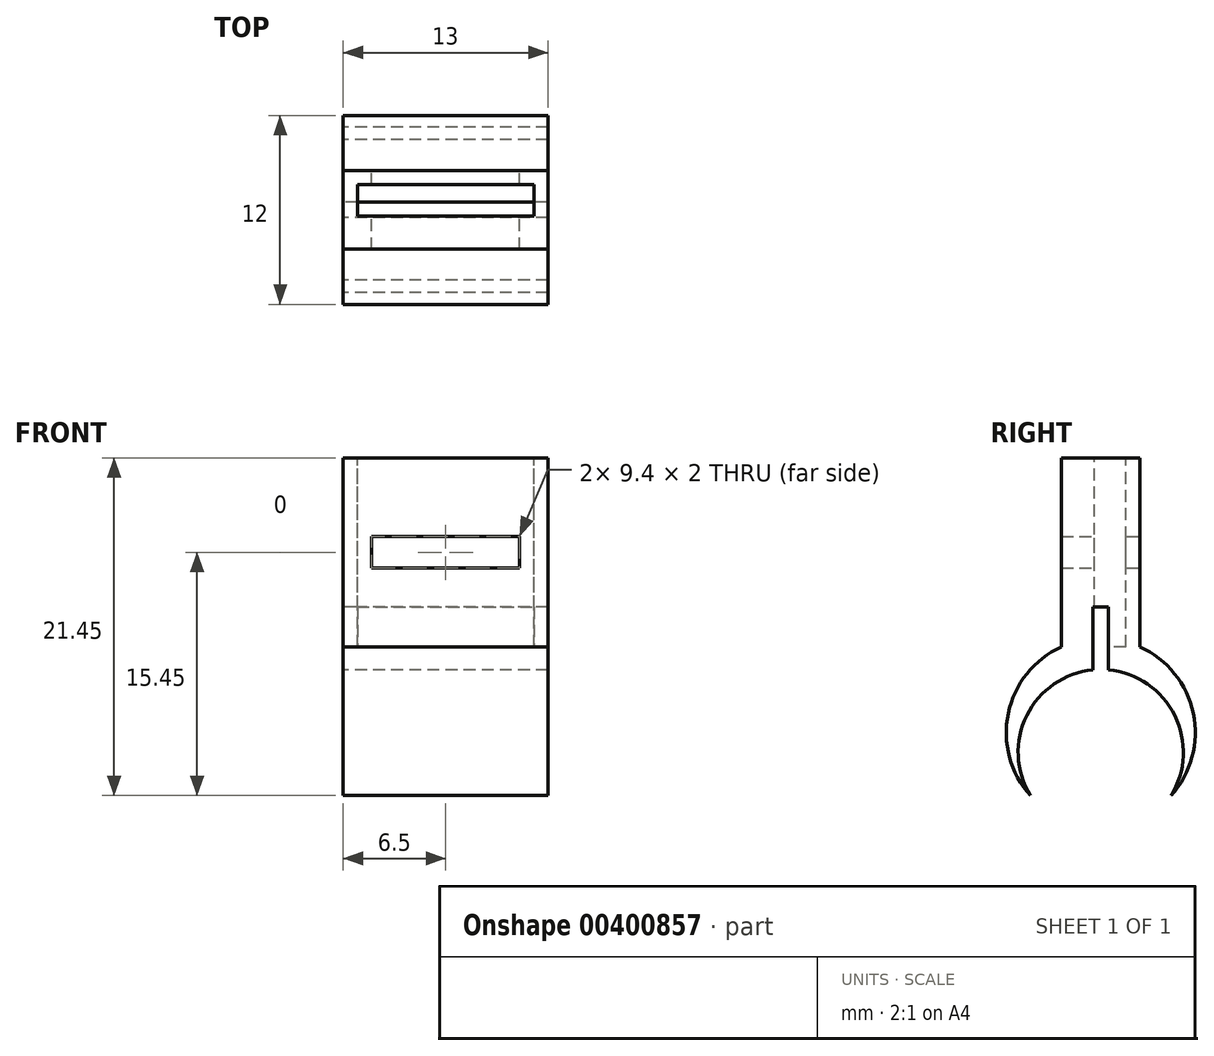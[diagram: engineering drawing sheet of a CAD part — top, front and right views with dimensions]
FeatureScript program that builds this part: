
annotation { "Feature Type Name" : "Feature", "Feature Type Description" : "" }
export const myFeature = defineFeature(function(context is Context, id is Id, definition is map)
    precondition{}
    {
        {
            var Q0;
            Q0=qCreatedBy(makeId("Top.planeOp"),FACE);
            var sketch = newSketch(context, id + "F0", { "sketchPlane" : qUnion([Q0])});
            skLineSegment(sketch, "E0.bottom", {"start": v(-6.5, 2.5) * mm, "end": v(6.5, 2.5) * mm});
            skLineSegment(sketch, "E0.top", {"start": v(-6.5, -2.5) * mm, "end": v(6.5, -2.5) * mm});
            skLineSegment(sketch, "E0.left", {"start": v(-6.5, 2.5) * mm, "end": v(-6.5, -2.5) * mm});
            skLineSegment(sketch, "E0.right", {"start": v(6.5, 2.5) * mm, "end": v(6.5, -2.5) * mm});
            skPoint(sketch, "E0.middle", {"position": v(0, 0) * mm});
            skSolve(sketch);
        }
        {
            var Q0;
            Q0 = qSketchRegion(id + "F0", true);
            extrude(context, id + "F1", {"entities" : qUnion([Q0]), "depth" : 12 * mm});
        }
        {
            var Q0;
            Q0=makeQuery(id+"F1.opExtrude","CAP_FACE",FACE,{"disambiguationData":[OSD([sQuery(id+"F0.wireOp",EDGE,"E0.bottom"),sQuery(id+"F0.wireOp",EDGE,"E0.top"),sQuery(id+"F0.wireOp",EDGE,"E0.left"),sQuery(id+"F0.wireOp",EDGE,"E0.right")])],"isStart":false});
            var sketch = newSketch(context, id + "F2", { "sketchPlane" : qUnion([Q0])});
            skLineSegment(sketch, "E1.bottom", {"start": v(-5.6, 1.6) * mm, "end": v(5.6, 1.6) * mm});
            skLineSegment(sketch, "E1.top", {"start": v(-5.6, -0.4) * mm, "end": v(5.6, -0.4) * mm});
            skLineSegment(sketch, "E1.left", {"start": v(-5.6, 1.6) * mm, "end": v(-5.6, -0.4) * mm});
            skLineSegment(sketch, "E1.right", {"start": v(5.6, 1.6) * mm, "end": v(5.6, -0.4) * mm});
            skSolve(sketch);
        }
        {
            var Q0;
            Q0 = qSketchRegion(id + "F2", true);
            extrude(context, id + "F3", {"entities" : qUnion([Q0]), "operationType" : NewBodyOperationType.REMOVE, "oppositeDirection" : true, "depth" : 12 * mm});
        }
        {
            var Q0;
            Q0=makeQuery(id+"F1.opExtrude","SWEPT_FACE",FACE,{"disambiguationData":[OSD([sQuery(id+"F0.wireOp",EDGE,"E0.bottom")])]});
            var sketch = newSketch(context, id + "F4", { "sketchPlane" : qUnion([Q0])});
            skLineSegment(sketch, "E2.bottom", {"start": v(-4.7, 7) * mm, "end": v(4.7, 7) * mm});
            skLineSegment(sketch, "E2.top", {"start": v(-4.7, 5) * mm, "end": v(4.7, 5) * mm});
            skLineSegment(sketch, "E2.left", {"start": v(-4.7, 7) * mm, "end": v(-4.7, 5) * mm});
            skLineSegment(sketch, "E2.right", {"start": v(4.7, 7) * mm, "end": v(4.7, 5) * mm});
            skSolve(sketch);
        }
        {
            var Q0;
            Q0 = qSketchRegion(id + "F4", true);
            extrude(context, id + "F5", {"entities" : qUnion([Q0]), "operationType" : NewBodyOperationType.REMOVE, "endBound" : BoundingType.THROUGH_ALL, "oppositeDirection" : true, "depth" : 25 * mm});
        }
        {
            var Q0;
            Q0=makeQuery(id+"F1.opExtrude","SWEPT_FACE",FACE,{"disambiguationData":[OSD([sQuery(id+"F0.wireOp",EDGE,"E0.left")])]});
            var sketch = newSketch(context, id + "F6", { "sketchPlane" : qUnion([Q0])});
            skCircle(sketch, "E3", {"center": v(0, -5.45) * mm, "radius": 6 * mm});
            skPoint(sketch, "E3.centerSnap0", {"position": v(0, 0) * mm});
            skCircle(sketch, "E4", {"center": v(0, -6.7) * mm, "radius": 5.25 * mm});
            skSolve(sketch);
        }
        {
            var Q0;
            {var subQ1=sQuery(id+"F0.wireOp",EDGE,"E0.left");var subQ2=makeQuery(id+"F1.opExtrude","CAP_EDGE",EDGE,{"disambiguationData":[OSD([subQ1])],"isStart":true});Q0=makeQuery(id+"F6.imprint","IMPRINT",FACE,{"disambiguationData":[TD([[makeQuery(id+"F6.imprint","IMPRINT",EDGE,{"derivedFrom":subQ2}),-1.0]])]});}
            extrude(context, id + "F7", {"entities" : qUnion([Q0]), "operationType" : NewBodyOperationType.ADD, "oppositeDirection" : true, "depth" : 13 * mm});
        }
        {
            var Q0;
            {var subQ0=sQuery(id+"F0.wireOp",EDGE,"E0.left");Q0=makeQuery(id+"F7.boolean.opBoolean","MERGE",FACE,{"derivedFrom":[makeQuery(id+"F1.opExtrude","SWEPT_FACE",FACE,{"disambiguationData":[OSD([subQ0])]}),makeQuery(id+"F7.opExtrude","CAP_FACE",FACE,{"disambiguationData":[OSD([subQ0,sQuery(id+"F6.wireOp",EDGE,"E3"),sQuery(id+"F6.wireOp",EDGE,"E4")])],"isStart":true})]});}
            var sketch = newSketch(context, id + "F8", { "sketchPlane" : qUnion([Q0])});
            skLineSegment(sketch, "E5.bottom", {"start": v(-0.5, 2.52) * mm, "end": v(0.5, 2.52) * mm});
            skLineSegment(sketch, "E5.top", {"start": v(-0.5, -1.48) * mm, "end": v(0.5, -1.48) * mm});
            skLineSegment(sketch, "E5.left", {"start": v(-0.5, 2.52) * mm, "end": v(-0.5, -1.48) * mm});
            skLineSegment(sketch, "E5.right", {"start": v(0.5, 2.52) * mm, "end": v(0.5, -1.48) * mm});
            skPoint(sketch, "E5.middle", {"position": v(0, 0.52) * mm});
            skSolve(sketch);
        }
        {
            var Q0;
            Q0 = qSketchRegion(id + "F8", true);
            extrude(context, id + "F9", {"entities" : qUnion([Q0]), "operationType" : NewBodyOperationType.REMOVE, "endBound" : BoundingType.THROUGH_ALL, "oppositeDirection" : true, "depth" : 25 * mm});
        }
    });
